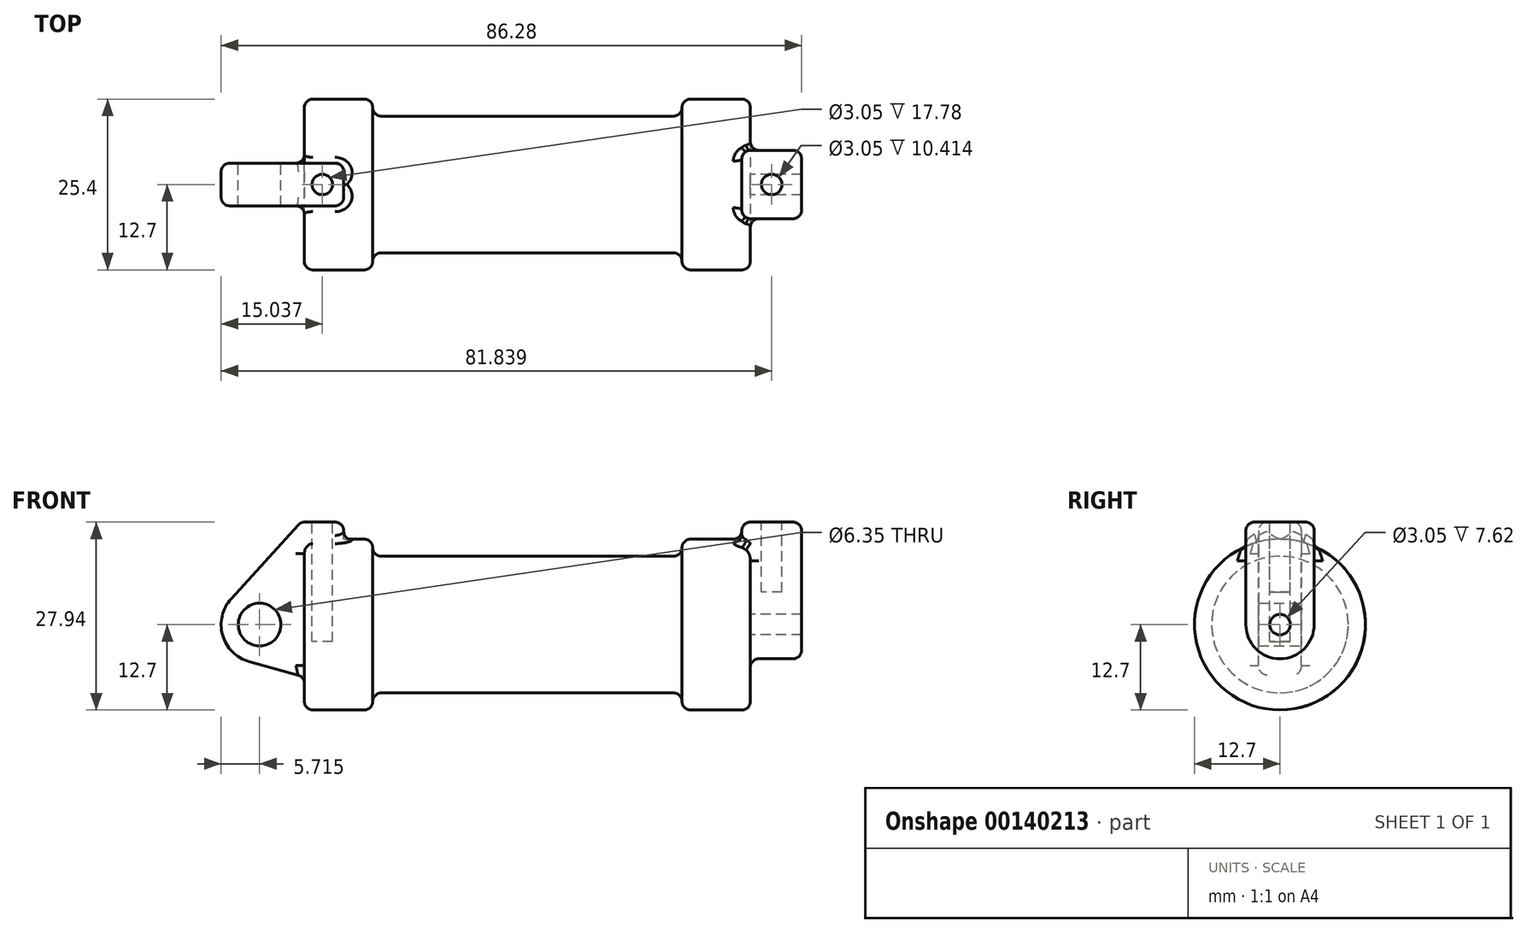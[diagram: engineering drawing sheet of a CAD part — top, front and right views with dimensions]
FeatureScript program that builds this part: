
annotation { "Feature Type Name" : "Feature", "Feature Type Description" : "" }
export const myFeature = defineFeature(function(context is Context, id is Id, definition is map)
    precondition{}
    {
        {
            var Q0;
            Q0=qCreatedBy(makeId("Front.planeOp"),FACE);
            var sketch = newSketch(context, id + "F0", { "sketchPlane" : qUnion([Q0])});
            skLineSegment(sketch, "E0", {"start": v(0, 0) * mm, "end": v(0, 12.7) * mm});
            skLineSegment(sketch, "E1", {"start": v(0, 12.7) * mm, "end": v(10.16, 12.7) * mm});
            skLineSegment(sketch, "E2", {"start": v(10.16, 12.7) * mm, "end": v(10.16, 10.16) * mm});
            skLineSegment(sketch, "E3", {"start": v(10.16, 10.16) * mm, "end": v(56.13, 10.16) * mm});
            skLineSegment(sketch, "E4", {"start": v(56.13, 10.16) * mm, "end": v(56.13, 12.7) * mm});
            skLineSegment(sketch, "E5", {"start": v(56.13, 12.7) * mm, "end": v(66.3, 12.7) * mm});
            skLineSegment(sketch, "E6", {"start": v(66.3, 12.7) * mm, "end": v(66.3, 0) * mm});
            skLineSegment(sketch, "E7", {"start": v(66.3, 0) * mm, "end": v(0, 0) * mm});
            skLineSegment(sketch, "E8", {"start": v(5.84, 15.24) * mm, "end": v(-0.5, 15.24) * mm});
            skLineSegment(sketch, "E9", {"start": v(-0.5, 15.24) * mm, "end": v(-10.88, 3.85) * mm});
            skLineSegment(sketch, "E10", {"start": v(0, 0) * mm, "end": v(-6.65, 0) * mm});
            skCircle(sketch, "E11", {"center": v(-6.65, 0) * mm, "radius": 5.72 * mm});
            skCircle(sketch, "E12", {"center": v(-6.65, 0) * mm, "radius": 3.18 * mm});
            skLineSegment(sketch, "E13", {"start": v(5.84, 15.24) * mm, "end": v(5.84, -9.4) * mm});
            skLineSegment(sketch, "E14", {"start": v(5.84, -9.4) * mm, "end": v(-8.18, -5.5) * mm});
            skSolve(sketch);
        }
        {
            var Q0;
            {var subQ0=sQuery(id+"F0.wireOp",EDGE,"E0");Q0=makeQuery(id+"F0.imprint","IMPRINT",FACE,{"disambiguationData":[TD([[makeQuery(id+"F0.imprint","IMPRINT",EDGE,{"derivedFrom":subQ0}),-1.0]])]});}
            var Q1;
            {var subQ0=sQuery(id+"F0.wireOp",EDGE,"E2");Q1=makeQuery(id+"F0.imprint","IMPRINT",FACE,{"disambiguationData":[TD([[makeQuery(id+"F0.imprint","IMPRINT",EDGE,{"derivedFrom":subQ0}),-1.0]])]});}
            var Q2;
            Q2=sQuery(id+"F0.wireOp",EDGE,"E7");
            revolve(context, id + "F1", {"entities" : qUnion([Q0, Q1]), "axis" : qUnion([Q2]), "revolveType" : RevolveType.FULL});
        }
        {
            var Q0;
            {var subQ0=sQuery(id+"F0.wireOp",EDGE,"E14");Q0=makeQuery(id+"F0.imprint","IMPRINT",FACE,{"disambiguationData":[TD([[makeQuery(id+"F0.imprint","IMPRINT",EDGE,{"derivedFrom":subQ0}),-1.0]])]});}
            var Q1;
            {var subQ4=sQuery(id+"F0.wireOp",EDGE,"E12");Q1=makeQuery(id+"F0.imprint","IMPRINT",FACE,{"disambiguationData":[TD([[makeQuery(id+"F0.imprint","IMPRINT",EDGE,{"derivedFrom":subQ4}),-1.0]])]});}
            var Q2;
            {var subQ3=sQuery(id+"F0.wireOp",EDGE,"E0");Q2=makeQuery(id+"F0.imprint","IMPRINT",FACE,{"disambiguationData":[TD([[makeQuery(id+"F0.imprint","IMPRINT",EDGE,{"derivedFrom":subQ3}),1.0]])]});}
            var Q3;
            {var subQ0=sQuery(id+"F0.wireOp",EDGE,"E0");Q3=makeQuery(id+"F0.imprint","IMPRINT",FACE,{"disambiguationData":[TD([[makeQuery(id+"F0.imprint","IMPRINT",EDGE,{"derivedFrom":subQ0}),-1.0]])]});}
            extrude(context, id + "F2", {"entities" : qUnion([Q0, Q1, Q2, Q3]), "endBound" : BoundingType.SYMMETRIC, "depth" : 6.35 * mm, "hasSecondDirection" : true, "secondDirectionOppositeDirection" : true, "secondDirectionDepth" : 3.17 * mm});
        }
        {
            var Q0;
            Q0=makeQuery(id+"F1.opRevolve","SWEPT_FACE",FACE,{"disambiguationData":[OSD([sQuery(id+"F0.wireOp",EDGE,"E6")])]});
            var sketch = newSketch(context, id + "F3", { "sketchPlane" : qUnion([Q0])});
            skCircle(sketch, "E15", {"center": v(0, 0) * mm, "radius": 1.52 * mm});
            skCircle(sketch, "E16", {"center": v(0, 0) * mm, "radius": 5.08 * mm});
            skLineSegment(sketch, "E17", {"start": v(-5.08, 0) * mm, "end": v(-5.08, 15.24) * mm});
            skLineSegment(sketch, "E18", {"start": v(-5.08, 15.24) * mm, "end": v(5.08, 15.24) * mm});
            skLineSegment(sketch, "E19", {"start": v(5.08, 15.24) * mm, "end": v(5.08, 0) * mm});
            skSolve(sketch);
        }
        {
            var Q0;
            Q0=makeQuery(id+"F3.imprint","IMPRINT",FACE,{"disambiguationData":[TD([[makeQuery(id+"F3.imprint","IMPRINT",EDGE,{"derivedFrom":sQuery(id+"F3.wireOp",EDGE,"E15")}),-1.0]])]});
            var Q1;
            {var subQ0=sQuery(id+"F3.wireOp",EDGE,"E17");var subQ1=sQuery(id+"F3.wireOp",EDGE,"E16");var subQ2=makeQuery(id+"F3.imprint","INTERSECT",VERTEX,{"derivedFrom":[subQ1,subQ0]});Q1=makeQuery(id+"F3.imprint","IMPRINT",FACE,{"disambiguationData":[TD([[makeQuery(id+"F3.imprint","IMPRINT",EDGE,{"disambiguationData":[TD([[subQ2,1.0]])],"derivedFrom":subQ1}),-1.0]])]});}
            var Q2;
            {var subQ0=sQuery(id+"F3.wireOp",EDGE,"E18");Q2=makeQuery(id+"F3.imprint","IMPRINT",FACE,{"disambiguationData":[TD([[makeQuery(id+"F3.imprint","IMPRINT",EDGE,{"derivedFrom":subQ0}),-1.0]])]});}
            extrude(context, id + "F4", {"entities" : qUnion([Q0, Q1, Q2]), "operationType" : NewBodyOperationType.ADD, "depth" : 7.62 * mm});
        }
        {
            var Q0;
            Q0=makeQuery(id+"F3.imprint","IMPRINT",FACE,{"disambiguationData":[TD([[makeQuery(id+"F3.imprint","IMPRINT",EDGE,{"derivedFrom":sQuery(id+"F3.wireOp",EDGE,"E15")}),-1.0]])]});
            var Q1;
            {var subQ0=sQuery(id+"F3.wireOp",EDGE,"E17");var subQ1=sQuery(id+"F3.wireOp",EDGE,"E16");var subQ2=makeQuery(id+"F3.imprint","INTERSECT",VERTEX,{"derivedFrom":[subQ1,subQ0]});Q1=makeQuery(id+"F3.imprint","IMPRINT",FACE,{"disambiguationData":[TD([[makeQuery(id+"F3.imprint","IMPRINT",EDGE,{"disambiguationData":[TD([[subQ2,1.0]])],"derivedFrom":subQ1}),-1.0]])]});}
            var Q2;
            {var subQ0=sQuery(id+"F3.wireOp",EDGE,"E18");Q2=makeQuery(id+"F3.imprint","IMPRINT",FACE,{"disambiguationData":[TD([[makeQuery(id+"F3.imprint","IMPRINT",EDGE,{"derivedFrom":subQ0}),-1.0]])]});}
            var Q3;
            Q3=makeQuery(id+"F3.imprint","IMPRINT",FACE,{"disambiguationData":[TD([[makeQuery(id+"F3.imprint","IMPRINT",EDGE,{"derivedFrom":sQuery(id+"F3.wireOp",EDGE,"E15")}),1.0]])]});
            extrude(context, id + "F5", {"entities" : qUnion([Q0, Q1, Q2, Q3]), "operationType" : NewBodyOperationType.ADD, "oppositeDirection" : true, "depth" : 1.27 * mm});
        }
        {
            var Q0;
            Q0=makeQuery(id+"F2.opExtrude","SWEPT_FACE",FACE,{"disambiguationData":[OSD([sQuery(id+"F0.wireOp",EDGE,"E8")])]});
            var sketch = newSketch(context, id + "F6", { "sketchPlane" : qUnion([Q0])});
            skCircle(sketch, "E20", {"center": v(2.67, 0) * mm, "radius": 1.52 * mm});
            skLineSegment(sketch, "E21", {"start": v(2.67, 0) * mm, "end": v(2.67, 3.18) * mm, "construction": true});
            skLineSegment(sketch, "E22", {"start": v(2.67, 0) * mm, "end": v(5.84, 0) * mm, "construction": true});
            skSolve(sketch);
        }
        {
            var Q0;
            Q0=makeQuery(id+"F6.imprint","IMPRINT",FACE,{"disambiguationData":[TD([[makeQuery(id+"F6.imprint","IMPRINT",EDGE,{"derivedFrom":sQuery(id+"F6.wireOp",EDGE,"E20")}),1.0]])]});
            var Q1;
            Q1=sQuery(id+"F6.wireOp",EDGE,"E20");
            extrude(context, id + "F7", {"entities" : qUnion([Q0]), "operationType" : NewBodyOperationType.REMOVE, "surfaceEntities" : qUnion([Q1]), "oppositeDirection" : true, "depth" : 17.78 * mm});
        }
        {
            var Q0;
            {var subQ0=sQuery(id+"F3.wireOp",EDGE,"E18");Q0=makeQuery(id+"F5.boolean.opBoolean","MERGE",FACE,{"derivedFrom":[makeQuery(id+"F4.opExtrude","SWEPT_FACE",FACE,{"disambiguationData":[OSD([subQ0])]}),makeQuery(id+"F5.opExtrude","SWEPT_FACE",FACE,{"disambiguationData":[OSD([subQ0])]})]});}
            var sketch = newSketch(context, id + "F8", { "sketchPlane" : qUnion([Q0])});
            skCircle(sketch, "E23", {"center": v(69.47, 0) * mm, "radius": 1.52 * mm});
            skLineSegment(sketch, "E24", {"start": v(69.47, 0) * mm, "end": v(69.47, 5.08) * mm, "construction": true});
            skLineSegment(sketch, "E25", {"start": v(69.47, 0) * mm, "end": v(73.91, 0) * mm, "construction": true});
            skSolve(sketch);
        }
        {
            var Q0;
            Q0=makeQuery(id+"F8.imprint","IMPRINT",FACE,{"disambiguationData":[TD([[makeQuery(id+"F8.imprint","IMPRINT",EDGE,{"derivedFrom":sQuery(id+"F8.wireOp",EDGE,"E23")}),1.0]])]});
            var Q1;
            Q1=sQuery(id+"F8.wireOp",EDGE,"E23");
            extrude(context, id + "F9", {"entities" : qUnion([Q0]), "operationType" : NewBodyOperationType.REMOVE, "surfaceEntities" : qUnion([Q1]), "oppositeDirection" : true, "depth" : 10.4 * mm});
        }
        {
            var Q0;
            Q0=makeQuery(id+"F2.opExtrude","SWEPT_BODY",BODY,{"disambiguationData":[OSD([sQuery(id+"F0.wireOp",EDGE,"E8"),sQuery(id+"F0.wireOp",EDGE,"E9"),sQuery(id+"F0.wireOp",EDGE,"E11"),sQuery(id+"F0.wireOp",EDGE,"E12"),sQuery(id+"F0.wireOp",EDGE,"E13"),sQuery(id+"F0.wireOp",EDGE,"E14")])]});
            var Q1;
            Q1=makeQuery(id+"F1.opRevolve","SWEPT_BODY",BODY,{"disambiguationData":[OSD([sQuery(id+"F0.wireOp",EDGE,"E0"),sQuery(id+"F0.wireOp",EDGE,"E1"),sQuery(id+"F0.wireOp",EDGE,"E2"),sQuery(id+"F0.wireOp",EDGE,"E3"),sQuery(id+"F0.wireOp",EDGE,"E4"),sQuery(id+"F0.wireOp",EDGE,"E5"),sQuery(id+"F0.wireOp",EDGE,"E6"),sQuery(id+"F0.wireOp",EDGE,"E7")])]});
            booleanBodies(context, id + "F10", {"operationType" : BooleanOperationType.UNION, "tools" : qUnion([Q0, Q1])});
        }
        {
            var Q0;
            Q0=makeQuery(id+"F4.boolean.opBoolean","SPLIT",EDGE,{"disambiguationData":[OD(1.0)],"derivedFrom":makeQuery(id+"F1.opRevolve","SWEPT_EDGE",EDGE,{"disambiguationData":[OSD([sQuery(id+"F0.wireOp",EDGE,"E5"),sQuery(id+"F0.wireOp",EDGE,"E6")])]})});
            var Q1;
            Q1=makeQuery(id+"F1.opRevolve","SWEPT_EDGE",EDGE,{"disambiguationData":[OSD([sQuery(id+"F0.wireOp",EDGE,"E4"),sQuery(id+"F0.wireOp",EDGE,"E5")])]});
            var Q2;
            Q2=makeQuery(id+"F1.opRevolve","SWEPT_EDGE",EDGE,{"disambiguationData":[OSD([sQuery(id+"F0.wireOp",EDGE,"E3"),sQuery(id+"F0.wireOp",EDGE,"E4")])]});
            var Q3;
            Q3=makeQuery(id+"F1.opRevolve","SWEPT_EDGE",EDGE,{"disambiguationData":[OSD([sQuery(id+"F0.wireOp",EDGE,"E2"),sQuery(id+"F0.wireOp",EDGE,"E3")])]});
            var Q4;
            Q4=makeQuery(id+"F1.opRevolve","SWEPT_EDGE",EDGE,{"disambiguationData":[OSD([sQuery(id+"F0.wireOp",EDGE,"E1"),sQuery(id+"F0.wireOp",EDGE,"E2")])]});
            var Q5;
            Q5=makeQuery(id+"F1.opRevolve","SWEPT_EDGE",EDGE,{"disambiguationData":[OSD([sQuery(id+"F0.wireOp",EDGE,"E0"),sQuery(id+"F0.wireOp",EDGE,"E1")])]});
            fillet(context, id + "F11", {"entities" : qUnion([Q0, Q1, Q2, Q3, Q4, Q5]), "radius" : 1.27 * mm, "tangentPropagation" : true, "allowEdgeOverflow" : false});
        }
        {
            var Q0;
            Q0=makeQuery(id+"F4.opExtrude","CAP_EDGE",EDGE,{"disambiguationData":[OSD([sQuery(id+"F3.wireOp",EDGE,"E18")])],"isStart":false});
            var Q1;
            {var subQ0=sQuery(id+"F3.wireOp",EDGE,"E19");var subQ1=sQuery(id+"F3.wireOp",EDGE,"E18");Q1=makeQuery(id+"F5.boolean.opBoolean","MERGE",EDGE,{"derivedFrom":[makeQuery(id+"F4.opExtrude","SWEPT_EDGE",EDGE,{"disambiguationData":[OSD([subQ1,subQ0])]}),makeQuery(id+"F5.opExtrude","SWEPT_EDGE",EDGE,{"disambiguationData":[OSD([subQ1,subQ0])]})]});}
            var Q2;
            Q2=makeQuery(id+"F5.opExtrude","CAP_EDGE",EDGE,{"disambiguationData":[OSD([sQuery(id+"F3.wireOp",EDGE,"E18")])],"isStart":false});
            var Q3;
            {var subQ0=sQuery(id+"F3.wireOp",EDGE,"E18");var subQ1=sQuery(id+"F3.wireOp",EDGE,"E17");Q3=makeQuery(id+"F5.boolean.opBoolean","MERGE",EDGE,{"derivedFrom":[makeQuery(id+"F4.opExtrude","SWEPT_EDGE",EDGE,{"disambiguationData":[OSD([subQ1,subQ0])]}),makeQuery(id+"F5.opExtrude","SWEPT_EDGE",EDGE,{"disambiguationData":[OSD([subQ1,subQ0])]})]});}
            var Q4;
            Q4=makeQuery(id+"F4.opExtrude","CAP_EDGE",EDGE,{"disambiguationData":[OSD([sQuery(id+"F3.wireOp",EDGE,"E19")])],"isStart":false});
            var Q5;
            {var subQ0=sQuery(id+"F3.wireOp",EDGE,"E16");var subQ1=sQuery(id+"F3.wireOp",EDGE,"E19");Q5=makeQuery(id+"F4.boolean.opBoolean","SPLIT",EDGE,{"disambiguationData":[TD([makeQuery(id+"F4.opExtrude","SWEPT_FACE",FACE,{"disambiguationData":[OSD([subQ0])]})])],"derivedFrom":makeQuery(id+"F4.opExtrude","CAP_EDGE",EDGE,{"disambiguationData":[OSD([subQ1])],"isStart":true})});}
            var Q6;
            Q6=makeQuery(id+"F5.opExtrude","CAP_EDGE",EDGE,{"disambiguationData":[OSD([sQuery(id+"F3.wireOp",EDGE,"E19")])],"isStart":false});
            var Q7;
            {var subQ0=sQuery(id+"F3.wireOp",EDGE,"E19");Q7=makeQuery(id+"F11.opFillet","BLEND_EDGE",EDGE,{"blendedFrom":[makeQuery(id+"F4.boolean.opBoolean","SPLIT",EDGE,{"disambiguationData":[OD(1.0)],"derivedFrom":makeQuery(id+"F1.opRevolve","SWEPT_EDGE",EDGE,{"disambiguationData":[OSD([sQuery(id+"F0.wireOp",EDGE,"E5"),sQuery(id+"F0.wireOp",EDGE,"E6")])]})}),makeQuery(id+"F5.boolean.opBoolean","MERGE",FACE,{"derivedFrom":[makeQuery(id+"F4.opExtrude","SWEPT_FACE",FACE,{"disambiguationData":[OSD([subQ0])]}),makeQuery(id+"F5.opExtrude","SWEPT_FACE",FACE,{"disambiguationData":[OSD([subQ0])]})]})],"blendedInto":[makeQuery(id+"F5.boolean.opBoolean","MERGE",FACE,{"derivedFrom":[makeQuery(id+"F4.opExtrude","SWEPT_FACE",FACE,{"disambiguationData":[OSD([subQ0])]}),makeQuery(id+"F5.opExtrude","SWEPT_FACE",FACE,{"disambiguationData":[OSD([subQ0])]})]})]});}
            var Q8;
            Q8=makeQuery(id+"F5.boolean.opBoolean","INTERSECT",EDGE,{"derivedFrom":[makeQuery(id+"F1.opRevolve","SWEPT_FACE",FACE,{"disambiguationData":[OSD([sQuery(id+"F0.wireOp",EDGE,"E5")])]}),makeQuery(id+"F5.opExtrude","CAP_FACE",FACE,{"disambiguationData":[OSD([sQuery(id+"F3.wireOp",EDGE,"E16"),sQuery(id+"F3.wireOp",EDGE,"E17"),sQuery(id+"F3.wireOp",EDGE,"E18"),sQuery(id+"F3.wireOp",EDGE,"E19")])],"isStart":false})]});
            var Q9;
            Q9=makeQuery(id+"F5.opExtrude","CAP_EDGE",EDGE,{"disambiguationData":[OSD([sQuery(id+"F3.wireOp",EDGE,"E17")])],"isStart":false});
            fillet(context, id + "F12", {"entities" : qUnion([Q0, Q1, Q2, Q3, Q4, Q5, Q6, Q7, Q8, Q9]), "radius" : 1.27 * mm, "tangentPropagation" : true, "allowEdgeOverflow" : false});
        }
        {
            var Q0;
            Q0=makeQuery(id+"F2.opExtrude","CAP_EDGE",EDGE,{"disambiguationData":[OSD([sQuery(id+"F0.wireOp",EDGE,"E11")])],"isStart":true});
            var Q1;
            Q1=makeQuery(id+"F10.opBoolean","INTERSECT",EDGE,{"derivedFrom":[makeQuery(id+"F1.opRevolve","SWEPT_FACE",FACE,{"disambiguationData":[OSD([sQuery(id+"F0.wireOp",EDGE,"E0")])]}),makeQuery(id+"F2.opExtrude","CAP_FACE",FACE,{"disambiguationData":[OSD([sQuery(id+"F0.wireOp",EDGE,"E8"),sQuery(id+"F0.wireOp",EDGE,"E9"),sQuery(id+"F0.wireOp",EDGE,"E11"),sQuery(id+"F0.wireOp",EDGE,"E12"),sQuery(id+"F0.wireOp",EDGE,"E13"),sQuery(id+"F0.wireOp",EDGE,"E14")])],"isStart":true})]});
            var Q2;
            Q2=makeQuery(id+"F2.opExtrude","CAP_EDGE",EDGE,{"disambiguationData":[OSD([sQuery(id+"F0.wireOp",EDGE,"E8")])],"isStart":true});
            var Q3;
            Q3=makeQuery(id+"F2.opExtrude","CAP_EDGE",EDGE,{"disambiguationData":[OSD([sQuery(id+"F0.wireOp",EDGE,"E13")])],"isStart":true});
            var Q4;
            Q4=makeQuery(id+"F2.opExtrude","SWEPT_EDGE",EDGE,{"disambiguationData":[OSD([sQuery(id+"F0.wireOp",EDGE,"E8"),sQuery(id+"F0.wireOp",EDGE,"E13")])]});
            var Q5;
            Q5=makeQuery(id+"F2.opExtrude","CAP_EDGE",EDGE,{"disambiguationData":[OSD([sQuery(id+"F0.wireOp",EDGE,"E13")])],"isStart":false});
            var Q6;
            Q6=makeQuery(id+"F2.opExtrude","CAP_EDGE",EDGE,{"disambiguationData":[OSD([sQuery(id+"F0.wireOp",EDGE,"E8")])],"isStart":false});
            var Q7;
            Q7=makeQuery(id+"F2.opExtrude","CAP_EDGE",EDGE,{"disambiguationData":[OSD([sQuery(id+"F0.wireOp",EDGE,"E9")])],"isStart":false});
            var Q8;
            Q8=makeQuery(id+"F2.opExtrude","SWEPT_EDGE",EDGE,{"disambiguationData":[OSD([sQuery(id+"F0.wireOp",EDGE,"E8"),sQuery(id+"F0.wireOp",EDGE,"E9")])]});
            var Q9;
            Q9=makeQuery(id+"F2.opExtrude","CAP_EDGE",EDGE,{"disambiguationData":[OSD([sQuery(id+"F0.wireOp",EDGE,"E14")])],"isStart":true});
            var Q10;
            Q10=makeQuery(id+"F2.opExtrude","CAP_EDGE",EDGE,{"disambiguationData":[OSD([sQuery(id+"F0.wireOp",EDGE,"E14")])],"isStart":false});
            var Q11;
            Q11=makeQuery(id+"F2.opExtrude","CAP_EDGE",EDGE,{"disambiguationData":[OSD([sQuery(id+"F0.wireOp",EDGE,"E11")])],"isStart":false});
            var Q12;
            Q12=makeQuery(id+"F10.opBoolean","INTERSECT",EDGE,{"derivedFrom":[makeQuery(id+"F1.opRevolve","SWEPT_FACE",FACE,{"disambiguationData":[OSD([sQuery(id+"F0.wireOp",EDGE,"E0")])]}),makeQuery(id+"F2.opExtrude","CAP_FACE",FACE,{"disambiguationData":[OSD([sQuery(id+"F0.wireOp",EDGE,"E8"),sQuery(id+"F0.wireOp",EDGE,"E9"),sQuery(id+"F0.wireOp",EDGE,"E11"),sQuery(id+"F0.wireOp",EDGE,"E12"),sQuery(id+"F0.wireOp",EDGE,"E13"),sQuery(id+"F0.wireOp",EDGE,"E14")])],"isStart":false})]});
            var Q13;
            Q13=makeQuery(id+"F10.opBoolean","INTERSECT",EDGE,{"derivedFrom":[makeQuery(id+"F2.opExtrude","CAP_FACE",FACE,{"disambiguationData":[OSD([sQuery(id+"F0.wireOp",EDGE,"E8"),sQuery(id+"F0.wireOp",EDGE,"E9"),sQuery(id+"F0.wireOp",EDGE,"E11"),sQuery(id+"F0.wireOp",EDGE,"E12"),sQuery(id+"F0.wireOp",EDGE,"E13"),sQuery(id+"F0.wireOp",EDGE,"E14")])],"isStart":false}),makeQuery(id+"F1.opRevolve","SWEPT_FACE",FACE,{"disambiguationData":[OSD([sQuery(id+"F0.wireOp",EDGE,"E1")])]})]});
            var Q14;
            Q14=makeQuery(id+"F11.opFillet","BLEND_EDGE",EDGE,{"blendedFrom":[makeQuery(id+"F1.opRevolve","SWEPT_EDGE",EDGE,{"disambiguationData":[OSD([sQuery(id+"F0.wireOp",EDGE,"E0"),sQuery(id+"F0.wireOp",EDGE,"E1")])]}),makeQuery(id+"F2.opExtrude","CAP_FACE",FACE,{"disambiguationData":[OSD([sQuery(id+"F0.wireOp",EDGE,"E8"),sQuery(id+"F0.wireOp",EDGE,"E9"),sQuery(id+"F0.wireOp",EDGE,"E11"),sQuery(id+"F0.wireOp",EDGE,"E12"),sQuery(id+"F0.wireOp",EDGE,"E13"),sQuery(id+"F0.wireOp",EDGE,"E14")])],"isStart":false})],"blendedInto":[makeQuery(id+"F2.opExtrude","CAP_FACE",FACE,{"disambiguationData":[OSD([sQuery(id+"F0.wireOp",EDGE,"E8"),sQuery(id+"F0.wireOp",EDGE,"E9"),sQuery(id+"F0.wireOp",EDGE,"E11"),sQuery(id+"F0.wireOp",EDGE,"E12"),sQuery(id+"F0.wireOp",EDGE,"E13"),sQuery(id+"F0.wireOp",EDGE,"E14")])],"isStart":false})]});
            var Q15;
            Q15=makeQuery(id+"F2.opExtrude","CAP_EDGE",EDGE,{"disambiguationData":[OSD([sQuery(id+"F0.wireOp",EDGE,"E9")])],"isStart":true});
            var Q16;
            Q16=makeQuery(id+"F10.opBoolean","INTERSECT",EDGE,{"derivedFrom":[makeQuery(id+"F2.opExtrude","CAP_FACE",FACE,{"disambiguationData":[OSD([sQuery(id+"F0.wireOp",EDGE,"E8"),sQuery(id+"F0.wireOp",EDGE,"E9"),sQuery(id+"F0.wireOp",EDGE,"E11"),sQuery(id+"F0.wireOp",EDGE,"E12"),sQuery(id+"F0.wireOp",EDGE,"E13"),sQuery(id+"F0.wireOp",EDGE,"E14")])],"isStart":true}),makeQuery(id+"F1.opRevolve","SWEPT_FACE",FACE,{"disambiguationData":[OSD([sQuery(id+"F0.wireOp",EDGE,"E1")])]})]});
            var Q17;
            Q17=makeQuery(id+"F11.opFillet","BLEND_EDGE",EDGE,{"blendedFrom":[makeQuery(id+"F1.opRevolve","SWEPT_EDGE",EDGE,{"disambiguationData":[OSD([sQuery(id+"F0.wireOp",EDGE,"E0"),sQuery(id+"F0.wireOp",EDGE,"E1")])]}),makeQuery(id+"F2.opExtrude","CAP_FACE",FACE,{"disambiguationData":[OSD([sQuery(id+"F0.wireOp",EDGE,"E8"),sQuery(id+"F0.wireOp",EDGE,"E9"),sQuery(id+"F0.wireOp",EDGE,"E11"),sQuery(id+"F0.wireOp",EDGE,"E12"),sQuery(id+"F0.wireOp",EDGE,"E13"),sQuery(id+"F0.wireOp",EDGE,"E14")])],"isStart":true})],"blendedInto":[makeQuery(id+"F2.opExtrude","CAP_FACE",FACE,{"disambiguationData":[OSD([sQuery(id+"F0.wireOp",EDGE,"E8"),sQuery(id+"F0.wireOp",EDGE,"E9"),sQuery(id+"F0.wireOp",EDGE,"E11"),sQuery(id+"F0.wireOp",EDGE,"E12"),sQuery(id+"F0.wireOp",EDGE,"E13"),sQuery(id+"F0.wireOp",EDGE,"E14")])],"isStart":true})]});
            var Q18;
            Q18=makeQuery(id+"F10.opBoolean","INTERSECT",EDGE,{"derivedFrom":[makeQuery(id+"F1.opRevolve","SWEPT_FACE",FACE,{"disambiguationData":[OSD([sQuery(id+"F0.wireOp",EDGE,"E0")])]}),makeQuery(id+"F2.opExtrude","SWEPT_FACE",FACE,{"disambiguationData":[OSD([sQuery(id+"F0.wireOp",EDGE,"E14")])]})]});
            fillet(context, id + "F13", {"entities" : qUnion([Q0, Q1, Q2, Q3, Q4, Q5, Q6, Q7, Q8, Q9, Q10, Q11, Q12, Q13, Q14, Q15, Q16, Q17, Q18]), "radius" : 1.27 * mm, "tangentPropagation" : true, "allowEdgeOverflow" : false});
        }
    });
